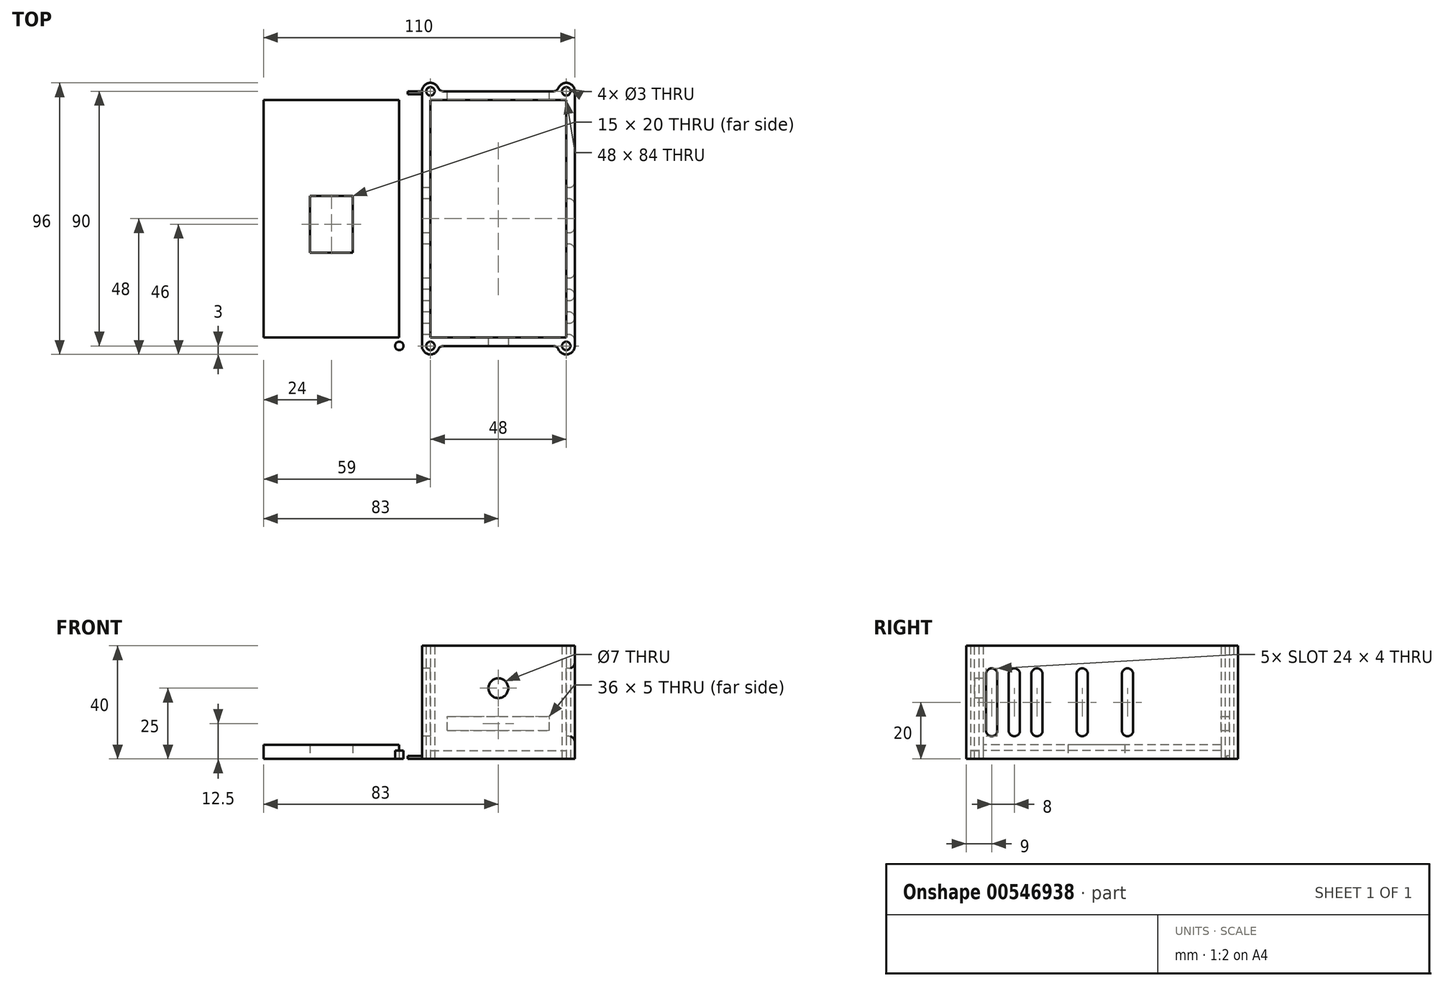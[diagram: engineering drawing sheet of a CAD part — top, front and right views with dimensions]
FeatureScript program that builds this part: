
annotation { "Feature Type Name" : "Feature", "Feature Type Description" : "" }
export const myFeature = defineFeature(function(context is Context, id is Id, definition is map)
    precondition{}
    {
        {
            var Q0;
            Q0=qCreatedBy(makeId("Top.planeOp"),FACE);
            var sketch = newSketch(context, id + "F0", { "sketchPlane" : qUnion([Q0])});
            skLineSegment(sketch, "E0.left", {"start": v(0, 0) * mm, "end": v(0, -90) * mm});
            skLineSegment(sketch, "E0.right", {"start": v(54, 0) * mm, "end": v(54, -90) * mm});
            skLineSegment(sketch, "E1.0", {"start": v(3, -3) * mm, "end": v(3, -87) * mm});
            skLineSegment(sketch, "E2.0", {"start": v(3, -3) * mm, "end": v(51, -3) * mm});
            skLineSegment(sketch, "E3.0", {"start": v(51, -3) * mm, "end": v(51, -87) * mm});
            skLineSegment(sketch, "E4.0", {"start": v(3, -87) * mm, "end": v(51, -87) * mm});
            skCircle(sketch, "E5", {"center": v(3, -90) * mm, "radius": 1.5 * mm});
            skArc(sketch, "E6", {"start": v(0, -90) * mm, "mid": v(3, -93) * mm, "end": v(6, -90) * mm});
            skCircle(sketch, "E7", {"center": v(51, -90) * mm, "radius": 1.5 * mm});
            skArc(sketch, "E8", {"start": v(48, -90) * mm, "mid": v(51, -93) * mm, "end": v(54, -90) * mm});
            skLineSegment(sketch, "E9.trimOffspring", {"start": v(6, -90) * mm, "end": v(48, -90) * mm});
            skCircle(sketch, "E10", {"center": v(3, 0) * mm, "radius": 1.5 * mm});
            skCircle(sketch, "E11", {"center": v(51, 0) * mm, "radius": 1.5 * mm});
            skArc(sketch, "E12", {"start": v(54, 0) * mm, "mid": v(51, 3) * mm, "end": v(48, 0) * mm});
            skArc(sketch, "E13", {"start": v(6, 0) * mm, "mid": v(3, 3) * mm, "end": v(0, 0) * mm});
            skLineSegment(sketch, "E14.trimOffspring", {"start": v(6, 0) * mm, "end": v(48, 0) * mm});
            skLineSegment(sketch, "E15", {"start": v(0, 0) * mm, "end": v(-2.5, 0) * mm, "construction": true});
            skCircle(sketch, "E16.MirrorC", {"center": v(-8, -90) * mm, "radius": 1.5 * mm});
            skCircle(sketch, "E17.MirrorC", {"center": v(-56, -90) * mm, "radius": 1.5 * mm});
            skCircle(sketch, "E18.MirrorC", {"center": v(-8, 0) * mm, "radius": 1.5 * mm});
            skArc(sketch, "E19.MirrorCS", {"start": v(-5, -90) * mm, "mid": v(-8, -93) * mm, "end": v(-11, -90) * mm});
            skLineSegment(sketch, "E20.MirrorCS", {"start": v(-8, -3) * mm, "end": v(-56, -3) * mm});
            skArc(sketch, "E21.MirrorCS", {"start": v(-53, -90) * mm, "mid": v(-56, -93) * mm, "end": v(-59, -90) * mm});
            skArc(sketch, "E22.MirrorCS", {"start": v(-11, 0) * mm, "mid": v(-8, 3) * mm, "end": v(-5, 0) * mm});
            skLineSegment(sketch, "E23.MirrorCS", {"start": v(-8, -87) * mm, "end": v(-56, -87) * mm});
            skLineSegment(sketch, "E24.MirrorCS", {"start": v(-11, 0) * mm, "end": v(-53, 0) * mm});
            skLineSegment(sketch, "E25.MirrorCS", {"start": v(-59, 0) * mm, "end": v(-59, -90) * mm});
            skLineSegment(sketch, "E26.MirrorCS", {"start": v(-8, -3) * mm, "end": v(-8, -87) * mm});
            skLineSegment(sketch, "E27.MirrorCS", {"start": v(-56, -3) * mm, "end": v(-56, -87) * mm});
            skLineSegment(sketch, "E28.MirrorCS", {"start": v(-11, -90) * mm, "end": v(-53, -90) * mm});
            skLineSegment(sketch, "E29.MirrorCS", {"start": v(-5, 0) * mm, "end": v(-5, -90) * mm});
            skCircle(sketch, "E30.MirrorC", {"center": v(-56, 0) * mm, "radius": 1.5 * mm});
            skArc(sketch, "E31.MirrorCS", {"start": v(-59, 0) * mm, "mid": v(-56, 3) * mm, "end": v(-53, 0) * mm});
            skLineSegment(sketch, "E32.0", {"start": v(-24.5, -57) * mm, "end": v(-39.5, -57) * mm});
            skLineSegment(sketch, "E33.0", {"start": v(-24.5, -37) * mm, "end": v(-39.5, -37) * mm});
            skLineSegment(sketch, "E34.0", {"start": v(-39.5, -37) * mm, "end": v(-39.5, -57) * mm});
            skLineSegment(sketch, "E35.0", {"start": v(-24.5, -37) * mm, "end": v(-24.5, -57) * mm});
            skLineSegment(sketch, "E36", {"start": v(-5, 0) * mm, "end": v(0, 0) * mm});
            skLineSegment(sketch, "E37.0", {"start": v(-5, -1) * mm, "end": v(0, -1) * mm});
            skSolve(sketch);
        }
        {
            var Q0;
            {var subQ0=sQuery(id+"F0.wireOp",EDGE,"E36");Q0=makeQuery(id+"F0.imprint","IMPRINT",FACE,{"disambiguationData":[TD([[makeQuery(id+"F0.imprint","IMPRINT",EDGE,{"derivedFrom":subQ0}),-1.0]])]});}
            extrude(context, id + "F1", {"entities" : qUnion([Q0]), "depth" : 1 * mm, "offsetDistance" : 25 * mm});
        }
        {
            var Q0;
            Q0=makeQuery(id+"F0.imprint","IMPRINT",FACE,{"disambiguationData":[TD([[makeQuery(id+"F0.imprint","IMPRINT",EDGE,{"derivedFrom":sQuery(id+"F0.wireOp",EDGE,"E16.MirrorC")}),1.0]])]});
            var Q1;
            Q1=makeQuery(id+"F0.imprint","IMPRINT",FACE,{"disambiguationData":[TD([[makeQuery(id+"F0.imprint","IMPRINT",EDGE,{"derivedFrom":sQuery(id+"F0.wireOp",EDGE,"E1.0")}),1.0]])]});
            extrude(context, id + "F2", {"entities" : qUnion([Q0, Q1]), "operationType" : NewBodyOperationType.ADD, "depth" : 3 * mm, "offsetDistance" : 25 * mm});
        }
        {
            var Q0;
            Q0=makeQuery(id+"F0.imprint","IMPRINT",FACE,{"disambiguationData":[TD([[makeQuery(id+"F0.imprint","IMPRINT",EDGE,{"derivedFrom":sQuery(id+"F0.wireOp",EDGE,"E20.MirrorCS")}),1.0]])]});
            extrude(context, id + "F3", {"entities" : qUnion([Q0]), "operationType" : NewBodyOperationType.ADD, "depth" : 5 * mm, "offsetDistance" : 25 * mm});
        }
        {
            var Q0;
            Q0=makeQuery(id+"F0.imprint","IMPRINT",FACE,{"disambiguationData":[TD([[makeQuery(id+"F0.imprint","IMPRINT",EDGE,{"derivedFrom":sQuery(id+"F0.wireOp",EDGE,"E0.right")}),-1.0]])]});
            extrude(context, id + "F4", {"entities" : qUnion([Q0]), "depth" : 40 * mm, "offsetDistance" : 25 * mm});
        }
        {
            var Q0;
            Q0=qCreatedBy(makeId("Front.planeOp"),FACE);
            var sketch = newSketch(context, id + "F5", { "sketchPlane" : qUnion([Q0])});
            skLineSegment(sketch, "E38", {"start": v(0, 0) * mm, "end": v(54, 0) * mm, "construction": true});
            skLineSegment(sketch, "E39.0", {"start": v(9, 10) * mm, "end": v(45, 10) * mm});
            skLineSegment(sketch, "E40.0", {"start": v(9, 15) * mm, "end": v(45, 15) * mm});
            skLineSegment(sketch, "E41", {"start": v(0, 0) * mm, "end": v(0, 15) * mm, "construction": true});
            skLineSegment(sketch, "E42.0", {"start": v(27, 0) * mm, "end": v(27, 15) * mm, "construction": true});
            skLineSegment(sketch, "E43.0", {"start": v(45, 10) * mm, "end": v(45, 15) * mm});
            skLineSegment(sketch, "E44.0", {"start": v(9, 10) * mm, "end": v(9, 15) * mm});
            skSolve(sketch);
        }
        {
            var Q0;
            Q0=makeQuery(id+"F5.imprint","IMPRINT",FACE,{"disambiguationData":[TD([[makeQuery(id+"F5.imprint","IMPRINT",EDGE,{"derivedFrom":sQuery(id+"F5.wireOp",EDGE,"E39.0")}),1.0]])]});
            extrude(context, id + "F6", {"entities" : qUnion([Q0]), "operationType" : NewBodyOperationType.REMOVE, "depth" : 5 * mm, "offsetDistance" : 25 * mm});
        }
        {
            var Q0;
            Q0=qCreatedBy(makeId("Front.planeOp"),FACE);
            cPlane(context, id + "F7", {"entities" : qUnion([Q0]), "cplaneType" : CPlaneType.OFFSET, "offset" : 100 * mm, "width" : 150 * mm, "height" : 150 * mm});
        }
        {
            var Q0;
            Q0=qCreatedBy(id+"F7.planeOp",FACE);
            var sketch = newSketch(context, id + "F8", { "sketchPlane" : qUnion([Q0])});
            skLineSegment(sketch, "E45", {"start": v(0, 0) * mm, "end": v(0, 40) * mm, "construction": true});
            skLineSegment(sketch, "E46", {"start": v(0, 40) * mm, "end": v(27, 40) * mm, "construction": true});
            skLineSegment(sketch, "E47", {"start": v(27, 40) * mm, "end": v(27, 25) * mm, "construction": true});
            skCircle(sketch, "E48", {"center": v(27, 25) * mm, "radius": 3.5 * mm});
            skSolve(sketch);
        }
        {
            var Q0;
            Q0=makeQuery(id+"F8.imprint","IMPRINT",FACE,{"disambiguationData":[TD([[makeQuery(id+"F8.imprint","IMPRINT",EDGE,{"derivedFrom":sQuery(id+"F8.wireOp",EDGE,"E48")}),1.0]])]});
            extrude(context, id + "F9", {"entities" : qUnion([Q0]), "operationType" : NewBodyOperationType.REMOVE, "oppositeDirection" : true, "depth" : 15 * mm, "offsetDistance" : 25 * mm});
        }
        {
            var Q0;
            Q0=qCreatedBy(makeId("Right.planeOp"),FACE);
            var sketch = newSketch(context, id + "F10", { "sketchPlane" : qUnion([Q0])});
            skLineSegment(sketch, "E49", {"start": v(0, 0) * mm, "end": v(0, 8) * mm, "construction": true});
            skLineSegment(sketch, "E50", {"start": v(0, 8) * mm, "end": v(0, 32) * mm, "construction": true});
            skLineSegment(sketch, "E51", {"start": v(0, 32) * mm, "end": v(-86, 32) * mm, "construction": true});
            skLineSegment(sketch, "E52.0", {"start": v(0, 30) * mm, "end": v(-86, 30) * mm, "construction": true});
            skLineSegment(sketch, "E53", {"start": v(-86, 30) * mm, "end": v(-86, 10) * mm});
            skLineSegment(sketch, "E54.0", {"start": v(-84, 30) * mm, "end": v(-84, 10) * mm, "construction": true});
            skLineSegment(sketch, "E55.MirrorCS", {"start": v(-82, 30) * mm, "end": v(-82, 10) * mm});
            skLineSegment(sketch, "E56.MirrorCS", {"start": v(-80, 30) * mm, "end": v(-80, 10) * mm, "construction": true});
            skLineSegment(sketch, "E57.MirrorCS", {"start": v(-76, 30) * mm, "end": v(-76, 10) * mm, "construction": true});
            skLineSegment(sketch, "E58.MirrorCS", {"start": v(-72, 30) * mm, "end": v(-72, 10) * mm, "construction": true});
            skLineSegment(sketch, "E59.MirrorCS", {"start": v(-68, 30) * mm, "end": v(-68, 10) * mm, "construction": true});
            skLineSegment(sketch, "E60.MirrorCS", {"start": v(-64, 30) * mm, "end": v(-64, 10) * mm, "construction": true});
            skLineSegment(sketch, "E61.MirrorCS", {"start": v(-60, 30) * mm, "end": v(-60, 10) * mm, "construction": true});
            skLineSegment(sketch, "E62.MirrorCS", {"start": v(-56, 30) * mm, "end": v(-56, 10) * mm, "construction": true});
            skLineSegment(sketch, "E63.MirrorCS", {"start": v(-48, 30) * mm, "end": v(-48, 10) * mm, "construction": true});
            skLineSegment(sketch, "E64.MirrorCS", {"start": v(-52, 30) * mm, "end": v(-52, 10) * mm, "construction": true});
            skLineSegment(sketch, "E65.MirrorCS", {"start": v(-44, 30) * mm, "end": v(-44, 10) * mm, "construction": true});
            skLineSegment(sketch, "E66.MirrorCS", {"start": v(-40, 30) * mm, "end": v(-40, 10) * mm, "construction": true});
            skLineSegment(sketch, "E67.MirrorCS", {"start": v(-36, 30) * mm, "end": v(-36, 10) * mm, "construction": true});
            skLineSegment(sketch, "E68.MirrorCS", {"start": v(-32, 30) * mm, "end": v(-32, 10) * mm, "construction": true});
            skLineSegment(sketch, "E69.MirrorCS", {"start": v(-28, 30) * mm, "end": v(-28, 10) * mm, "construction": true});
            skArc(sketch, "E70", {"start": v(-82, 30) * mm, "mid": v(-84, 32) * mm, "end": v(-86, 30) * mm});
            skArc(sketch, "E71", {"start": v(-86, 10) * mm, "mid": v(-84, 8) * mm, "end": v(-82, 10) * mm});
            skLineSegment(sketch, "E72.MirrorCS", {"start": v(-78, 30) * mm, "end": v(-78, 10) * mm});
            skArc(sketch, "E73.MirrorCS", {"start": v(-78, 30) * mm, "mid": v(-76, 32) * mm, "end": v(-74, 30) * mm});
            skLineSegment(sketch, "E74.MirrorCS", {"start": v(-74, 30) * mm, "end": v(-74, 10) * mm});
            skArc(sketch, "E75.MirrorCS", {"start": v(-74, 10) * mm, "mid": v(-76, 8) * mm, "end": v(-78, 10) * mm});
            skArc(sketch, "E76.MirrorCS", {"start": v(-66, 30) * mm, "mid": v(-68, 32) * mm, "end": v(-70, 30) * mm});
            skLineSegment(sketch, "E77.MirrorCS", {"start": v(-66, 30) * mm, "end": v(-66, 10) * mm});
            skLineSegment(sketch, "E78.MirrorCS", {"start": v(-70, 30) * mm, "end": v(-70, 10) * mm});
            skArc(sketch, "E79.MirrorCS", {"start": v(-70, 10) * mm, "mid": v(-68, 8) * mm, "end": v(-66, 10) * mm});
            skArc(sketch, "E80.MirrorCS", {"start": v(-58, 10) * mm, "mid": v(-60, 8) * mm, "end": v(-62, 10) * mm});
            skLineSegment(sketch, "E81.MirrorCS", {"start": v(-62, 30) * mm, "end": v(-62, 10) * mm});
            skLineSegment(sketch, "E82.MirrorCS", {"start": v(-58, 30) * mm, "end": v(-58, 10) * mm});
            skArc(sketch, "E83.MirrorCS", {"start": v(-62, 30) * mm, "mid": v(-60, 32) * mm, "end": v(-58, 30) * mm});
            skArc(sketch, "E84.MirrorCS", {"start": v(-46, 30) * mm, "mid": v(-44, 32) * mm, "end": v(-42, 30) * mm});
            skArc(sketch, "E85.MirrorCS", {"start": v(-50, 30) * mm, "mid": v(-52, 32) * mm, "end": v(-54, 30) * mm});
            skArc(sketch, "E86.MirrorCS", {"start": v(-34, 30) * mm, "mid": v(-36, 32) * mm, "end": v(-38, 30) * mm});
            skArc(sketch, "E87.MirrorCS", {"start": v(-30, 30) * mm, "mid": v(-28, 32) * mm, "end": v(-26, 30) * mm});
            skArc(sketch, "E88.MirrorCS", {"start": v(-38, 10) * mm, "mid": v(-36, 8) * mm, "end": v(-34, 10) * mm});
            skArc(sketch, "E89.MirrorCS", {"start": v(-42, 10) * mm, "mid": v(-44, 8) * mm, "end": v(-46, 10) * mm});
            skArc(sketch, "E90.MirrorCS", {"start": v(-54, 10) * mm, "mid": v(-52, 8) * mm, "end": v(-50, 10) * mm});
            skArc(sketch, "E91.MirrorCS", {"start": v(-26, 10) * mm, "mid": v(-28, 8) * mm, "end": v(-30, 10) * mm});
            skLineSegment(sketch, "E92.MirrorCS", {"start": v(-26, 30) * mm, "end": v(-26, 10) * mm});
            skLineSegment(sketch, "E93.MirrorCS", {"start": v(-30, 30) * mm, "end": v(-30, 10) * mm});
            skLineSegment(sketch, "E94.MirrorCS", {"start": v(-34, 30) * mm, "end": v(-34, 10) * mm});
            skLineSegment(sketch, "E95.MirrorCS", {"start": v(-38, 30) * mm, "end": v(-38, 10) * mm});
            skLineSegment(sketch, "E96.MirrorCS", {"start": v(-42, 30) * mm, "end": v(-42, 10) * mm});
            skLineSegment(sketch, "E97.MirrorCS", {"start": v(-46, 30) * mm, "end": v(-46, 10) * mm});
            skLineSegment(sketch, "E98.MirrorCS", {"start": v(-50, 30) * mm, "end": v(-50, 10) * mm});
            skLineSegment(sketch, "E99.MirrorCS", {"start": v(-54, 30) * mm, "end": v(-54, 10) * mm});
            skSolve(sketch);
        }
        {
            var Q0;
            Q0=makeQuery(id+"F10.imprint","IMPRINT",FACE,{"disambiguationData":[TD([[makeQuery(id+"F10.imprint","IMPRINT",EDGE,{"derivedFrom":sQuery(id+"F10.wireOp",EDGE,"E53")}),1.0]])]});
            var Q1;
            Q1=makeQuery(id+"F10.imprint","IMPRINT",FACE,{"disambiguationData":[TD([[makeQuery(id+"F10.imprint","IMPRINT",EDGE,{"derivedFrom":sQuery(id+"F10.wireOp",EDGE,"E72.MirrorCS")}),1.0]])]});
            var Q2;
            Q2=makeQuery(id+"F10.imprint","IMPRINT",FACE,{"disambiguationData":[TD([[makeQuery(id+"F10.imprint","IMPRINT",EDGE,{"derivedFrom":sQuery(id+"F10.wireOp",EDGE,"E76.MirrorCS")}),1.0]])]});
            var Q3;
            Q3=makeQuery(id+"F10.imprint","IMPRINT",FACE,{"disambiguationData":[TD([[makeQuery(id+"F10.imprint","IMPRINT",EDGE,{"derivedFrom":sQuery(id+"F10.wireOp",EDGE,"E80.MirrorCS")}),-1.0]])]});
            var Q4;
            Q4=makeQuery(id+"F10.imprint","IMPRINT",FACE,{"disambiguationData":[TD([[makeQuery(id+"F10.imprint","IMPRINT",EDGE,{"derivedFrom":sQuery(id+"F10.wireOp",EDGE,"E85.MirrorCS")}),1.0]])]});
            var Q5;
            Q5=makeQuery(id+"F10.imprint","IMPRINT",FACE,{"disambiguationData":[TD([[makeQuery(id+"F10.imprint","IMPRINT",EDGE,{"derivedFrom":sQuery(id+"F10.wireOp",EDGE,"E84.MirrorCS")}),-1.0]])]});
            var Q6;
            Q6=makeQuery(id+"F10.imprint","IMPRINT",FACE,{"disambiguationData":[TD([[makeQuery(id+"F10.imprint","IMPRINT",EDGE,{"derivedFrom":sQuery(id+"F10.wireOp",EDGE,"E86.MirrorCS")}),1.0]])]});
            var Q7;
            Q7=makeQuery(id+"F10.imprint","IMPRINT",FACE,{"disambiguationData":[TD([[makeQuery(id+"F10.imprint","IMPRINT",EDGE,{"derivedFrom":sQuery(id+"F10.wireOp",EDGE,"E87.MirrorCS")}),-1.0]])]});
            extrude(context, id + "F11", {"entities" : qUnion([Q0, Q1, Q2, Q3, Q4, Q5, Q6, Q7]), "operationType" : NewBodyOperationType.REMOVE, "depth" : 60 * mm, "offsetDistance" : 25 * mm});
        }
        {
            var Q0;
            Q0=makeQuery(id+"F4.opExtrude","SWEPT_EDGE",EDGE,{"disambiguationData":[OSD([sQuery(id+"F0.wireOp",EDGE,"E8"),sQuery(id+"F0.wireOp",EDGE,"E9.trimOffspring")])]});
            var Q1;
            Q1=makeQuery(id+"F4.opExtrude","SWEPT_EDGE",EDGE,{"disambiguationData":[OSD([sQuery(id+"F0.wireOp",EDGE,"E6"),sQuery(id+"F0.wireOp",EDGE,"E9.trimOffspring")])]});
            var Q2;
            Q2=makeQuery(id+"F11.boolean.opBoolean","INTERSECT",EDGE,{"derivedFrom":[makeQuery(id+"F4.opExtrude","SWEPT_FACE",FACE,{"disambiguationData":[OSD([sQuery(id+"F0.wireOp",EDGE,"E0.right")])]}),makeQuery(id+"F11.opExtrude","SWEPT_FACE",FACE,{"disambiguationData":[OSD([sQuery(id+"F10.wireOp",EDGE,"E55.MirrorCS")])]})]});
            var Q3;
            Q3=makeQuery(id+"F11.boolean.opBoolean","INTERSECT",EDGE,{"derivedFrom":[makeQuery(id+"F4.opExtrude","SWEPT_FACE",FACE,{"disambiguationData":[OSD([sQuery(id+"F0.wireOp",EDGE,"E0.right")])]}),makeQuery(id+"F11.opExtrude","SWEPT_FACE",FACE,{"disambiguationData":[OSD([sQuery(id+"F10.wireOp",EDGE,"E74.MirrorCS")])]})]});
            var Q4;
            Q4=makeQuery(id+"F11.boolean.opBoolean","INTERSECT",EDGE,{"derivedFrom":[makeQuery(id+"F4.opExtrude","SWEPT_FACE",FACE,{"disambiguationData":[OSD([sQuery(id+"F0.wireOp",EDGE,"E0.right")])]}),makeQuery(id+"F11.opExtrude","SWEPT_FACE",FACE,{"disambiguationData":[OSD([sQuery(id+"F10.wireOp",EDGE,"E77.MirrorCS")])]})]});
            var Q5;
            Q5=makeQuery(id+"F11.boolean.opBoolean","INTERSECT",EDGE,{"derivedFrom":[makeQuery(id+"F4.opExtrude","SWEPT_FACE",FACE,{"disambiguationData":[OSD([sQuery(id+"F0.wireOp",EDGE,"E0.right")])]}),makeQuery(id+"F11.opExtrude","SWEPT_FACE",FACE,{"disambiguationData":[OSD([sQuery(id+"F10.wireOp",EDGE,"E82.MirrorCS")])]})]});
            var Q6;
            Q6=makeQuery(id+"F11.boolean.opBoolean","INTERSECT",EDGE,{"derivedFrom":[makeQuery(id+"F4.opExtrude","SWEPT_FACE",FACE,{"disambiguationData":[OSD([sQuery(id+"F0.wireOp",EDGE,"E0.right")])]}),makeQuery(id+"F11.opExtrude","SWEPT_FACE",FACE,{"disambiguationData":[OSD([sQuery(id+"F10.wireOp",EDGE,"E98.MirrorCS")])]})]});
            var Q7;
            Q7=makeQuery(id+"F11.boolean.opBoolean","INTERSECT",EDGE,{"derivedFrom":[makeQuery(id+"F4.opExtrude","SWEPT_FACE",FACE,{"disambiguationData":[OSD([sQuery(id+"F0.wireOp",EDGE,"E0.right")])]}),makeQuery(id+"F11.opExtrude","SWEPT_FACE",FACE,{"disambiguationData":[OSD([sQuery(id+"F10.wireOp",EDGE,"E96.MirrorCS")])]})]});
            var Q8;
            Q8=makeQuery(id+"F11.boolean.opBoolean","INTERSECT",EDGE,{"derivedFrom":[makeQuery(id+"F4.opExtrude","SWEPT_FACE",FACE,{"disambiguationData":[OSD([sQuery(id+"F0.wireOp",EDGE,"E0.right")])]}),makeQuery(id+"F11.opExtrude","SWEPT_FACE",FACE,{"disambiguationData":[OSD([sQuery(id+"F10.wireOp",EDGE,"E94.MirrorCS")])]})]});
            var Q9;
            Q9=makeQuery(id+"F11.boolean.opBoolean","INTERSECT",EDGE,{"derivedFrom":[makeQuery(id+"F4.opExtrude","SWEPT_FACE",FACE,{"disambiguationData":[OSD([sQuery(id+"F0.wireOp",EDGE,"E0.right")])]}),makeQuery(id+"F11.opExtrude","SWEPT_FACE",FACE,{"disambiguationData":[OSD([sQuery(id+"F10.wireOp",EDGE,"E92.MirrorCS")])]})]});
            var Q10;
            Q10=makeQuery(id+"F11.boolean.opBoolean","COPY",EDGE,{"derivedFrom":makeQuery(id+"F11.opExtrude","CAP_EDGE",EDGE,{"disambiguationData":[OSD([sQuery(id+"F10.wireOp",EDGE,"E53")])],"isStart":true})});
            var Q11;
            Q11=makeQuery(id+"F11.boolean.opBoolean","COPY",EDGE,{"derivedFrom":makeQuery(id+"F11.opExtrude","CAP_EDGE",EDGE,{"disambiguationData":[OSD([sQuery(id+"F10.wireOp",EDGE,"E72.MirrorCS")])],"isStart":true})});
            var Q12;
            Q12=makeQuery(id+"F11.boolean.opBoolean","COPY",EDGE,{"derivedFrom":makeQuery(id+"F11.opExtrude","CAP_EDGE",EDGE,{"disambiguationData":[OSD([sQuery(id+"F10.wireOp",EDGE,"E78.MirrorCS")])],"isStart":true})});
            var Q13;
            Q13=makeQuery(id+"F11.boolean.opBoolean","COPY",EDGE,{"derivedFrom":makeQuery(id+"F11.opExtrude","CAP_EDGE",EDGE,{"disambiguationData":[OSD([sQuery(id+"F10.wireOp",EDGE,"E82.MirrorCS")])],"isStart":true})});
            var Q14;
            Q14=makeQuery(id+"F11.boolean.opBoolean","COPY",EDGE,{"derivedFrom":makeQuery(id+"F11.opExtrude","CAP_EDGE",EDGE,{"disambiguationData":[OSD([sQuery(id+"F10.wireOp",EDGE,"E98.MirrorCS")])],"isStart":true})});
            var Q15;
            Q15=makeQuery(id+"F11.boolean.opBoolean","COPY",EDGE,{"derivedFrom":makeQuery(id+"F11.opExtrude","CAP_EDGE",EDGE,{"disambiguationData":[OSD([sQuery(id+"F10.wireOp",EDGE,"E96.MirrorCS")])],"isStart":true})});
            var Q16;
            Q16=makeQuery(id+"F11.boolean.opBoolean","COPY",EDGE,{"derivedFrom":makeQuery(id+"F11.opExtrude","CAP_EDGE",EDGE,{"disambiguationData":[OSD([sQuery(id+"F10.wireOp",EDGE,"E94.MirrorCS")])],"isStart":true})});
            var Q17;
            Q17=makeQuery(id+"F11.boolean.opBoolean","COPY",EDGE,{"derivedFrom":makeQuery(id+"F11.opExtrude","CAP_EDGE",EDGE,{"disambiguationData":[OSD([sQuery(id+"F10.wireOp",EDGE,"E92.MirrorCS")])],"isStart":true})});
            var Q18;
            Q18=makeQuery(id+"F2.opExtrude","SWEPT_EDGE",EDGE,{"disambiguationData":[OSD([sQuery(id+"F0.wireOp",EDGE,"E24.MirrorCS"),sQuery(id+"F0.wireOp",EDGE,"E31.MirrorCS")])]});
            var Q19;
            Q19=makeQuery(id+"F2.opExtrude","SWEPT_EDGE",EDGE,{"disambiguationData":[OSD([sQuery(id+"F0.wireOp",EDGE,"E22.MirrorCS"),sQuery(id+"F0.wireOp",EDGE,"E24.MirrorCS")])]});
            var Q20;
            Q20=makeQuery(id+"F4.opExtrude","SWEPT_EDGE",EDGE,{"disambiguationData":[OSD([sQuery(id+"F0.wireOp",EDGE,"E12"),sQuery(id+"F0.wireOp",EDGE,"E14.trimOffspring")])]});
            var Q21;
            Q21=makeQuery(id+"F6.boolean.opBoolean","COPY",EDGE,{"derivedFrom":makeQuery(id+"F6.opExtrude","CAP_EDGE",EDGE,{"disambiguationData":[OSD([sQuery(id+"F5.wireOp",EDGE,"E39.0")])],"isStart":true})});
            var Q22;
            Q22=makeQuery(id+"F6.boolean.opBoolean","COPY",EDGE,{"derivedFrom":makeQuery(id+"F6.opExtrude","CAP_EDGE",EDGE,{"disambiguationData":[OSD([sQuery(id+"F5.wireOp",EDGE,"E40.0")])],"isStart":true})});
            var Q23;
            Q23=makeQuery(id+"F4.opExtrude","SWEPT_EDGE",EDGE,{"disambiguationData":[OSD([sQuery(id+"F0.wireOp",EDGE,"E13"),sQuery(id+"F0.wireOp",EDGE,"E14.trimOffspring")])]});
            var Q24;
            Q24=makeQuery(id+"F2.opExtrude","SWEPT_EDGE",EDGE,{"disambiguationData":[OSD([sQuery(id+"F0.wireOp",EDGE,"E19.MirrorCS"),sQuery(id+"F0.wireOp",EDGE,"E28.MirrorCS")])]});
            var Q25;
            Q25=makeQuery(id+"F2.opExtrude","SWEPT_EDGE",EDGE,{"disambiguationData":[OSD([sQuery(id+"F0.wireOp",EDGE,"E21.MirrorCS"),sQuery(id+"F0.wireOp",EDGE,"E28.MirrorCS")])]});
            fillet(context, id + "F12", {"entities" : qUnion([Q0, Q1, Q2, Q3, Q4, Q5, Q6, Q7, Q8, Q9, Q10, Q11, Q12, Q13, Q14, Q15, Q16, Q17, Q18, Q19, Q20, Q21, Q22, Q23, Q24, Q25]), "radius" : 2 * mm, "tangentPropagation" : true, "allowEdgeOverflow" : false});
        }
    });
